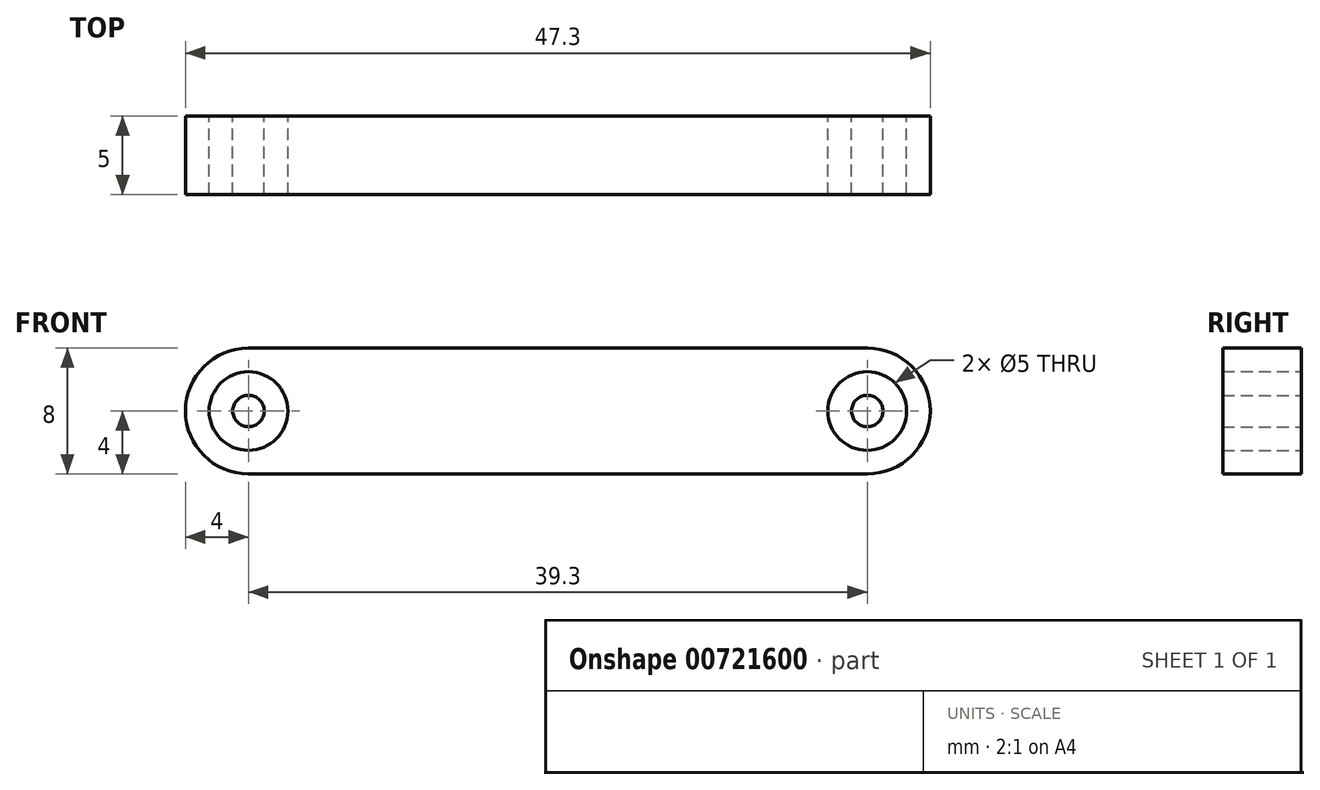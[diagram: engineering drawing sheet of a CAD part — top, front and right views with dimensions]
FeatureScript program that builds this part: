
annotation { "Feature Type Name" : "Feature", "Feature Type Description" : "" }
export const myFeature = defineFeature(function(context is Context, id is Id, definition is map)
    precondition{}
    {
        {
            var Q0;
            Q0=qCreatedBy(makeId("Front.planeOp"),FACE);
            var sketch = newSketch(context, id + "F0", { "sketchPlane" : qUnion([Q0])});
            skLineSegment(sketch, "E0.bottom", {"start": v(19.65, 4) * mm, "end": v(-19.65, 4) * mm});
            skLineSegment(sketch, "E0.top", {"start": v(19.65, -4) * mm, "end": v(-19.65, -4) * mm});
            skPoint(sketch, "E0.middle", {"position": v(0, 0) * mm});
            skArc(sketch, "E1", {"start": v(-19.65, 4) * mm, "mid": v(-23.65, 0) * mm, "end": v(-19.65, -4) * mm});
            skArc(sketch, "E2", {"start": v(19.65, -4) * mm, "mid": v(23.65, 0) * mm, "end": v(19.65, 4) * mm});
            skCircle(sketch, "E3", {"center": v(19.65, 0) * mm, "radius": 2.5 * mm});
            skCircle(sketch, "E4", {"center": v(19.65, 0) * mm, "radius": 1 * mm});
            skCircle(sketch, "E5", {"center": v(-19.65, 0) * mm, "radius": 2.5 * mm});
            skCircle(sketch, "E6", {"center": v(-19.65, 0) * mm, "radius": 1 * mm});
            skSolve(sketch);
        }
        {
            var Q0;
            Q0=makeQuery(id+"F0.imprint","IMPRINT",FACE,{"disambiguationData":[TD([[makeQuery(id+"F0.imprint","IMPRINT",EDGE,{"derivedFrom":sQuery(id+"F0.wireOp",EDGE,"E0.bottom")}),1.0]])]});
            var Q1;
            Q1=makeQuery(id+"F0.imprint","IMPRINT",FACE,{"disambiguationData":[TD([[makeQuery(id+"F0.imprint","IMPRINT",EDGE,{"derivedFrom":sQuery(id+"F0.wireOp",EDGE,"E6")}),1.0]])]});
            var Q2;
            Q2=makeQuery(id+"F0.imprint","IMPRINT",FACE,{"disambiguationData":[TD([[makeQuery(id+"F0.imprint","IMPRINT",EDGE,{"derivedFrom":sQuery(id+"F0.wireOp",EDGE,"E4")}),1.0]])]});
            extrude(context, id + "F1", {"entities" : qUnion([Q0, Q1, Q2]), "endBound" : BoundingType.SYMMETRIC, "depth" : 5 * mm, "offsetDistance" : 25.4 * mm});
        }
    });
